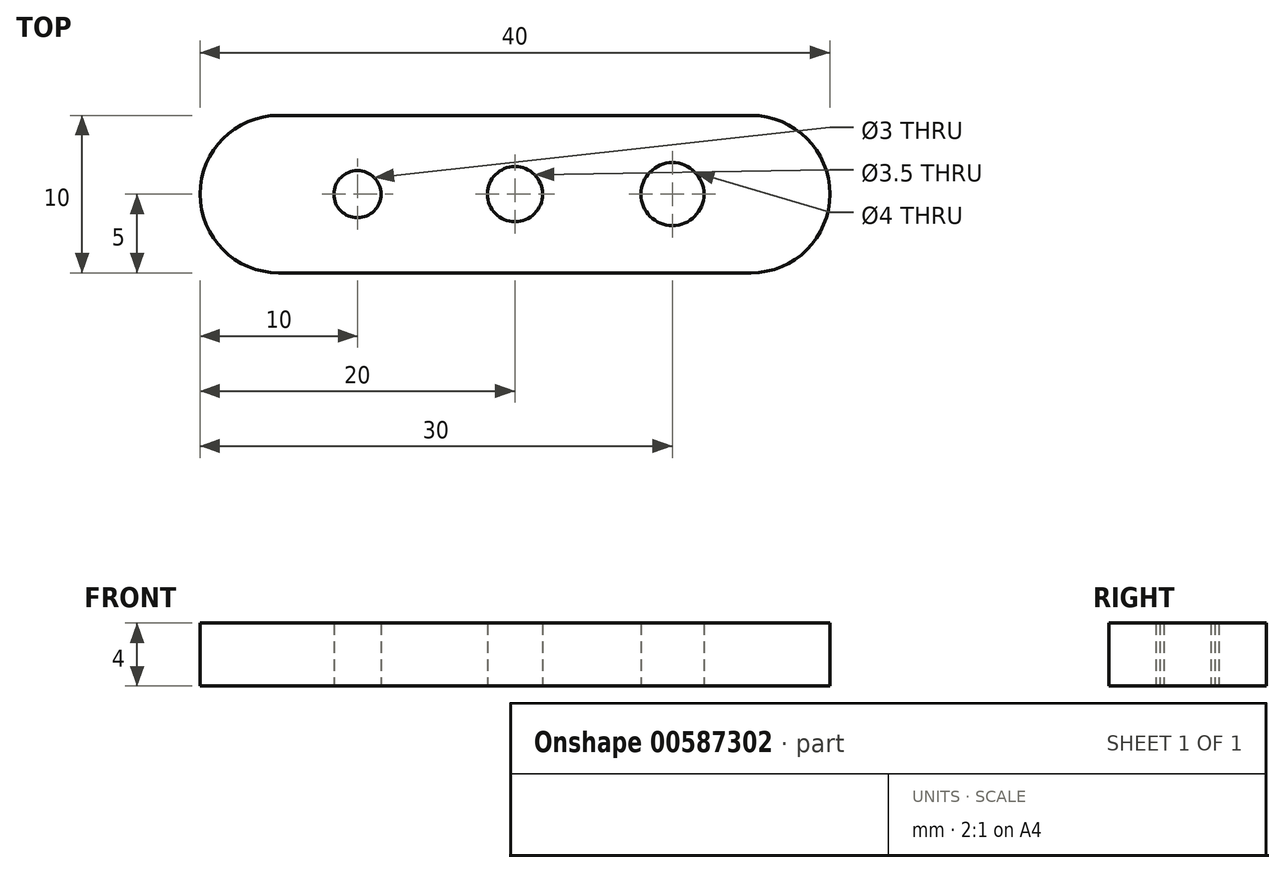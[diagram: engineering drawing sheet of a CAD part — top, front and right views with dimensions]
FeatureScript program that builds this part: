
annotation { "Feature Type Name" : "Feature", "Feature Type Description" : "" }
export const myFeature = defineFeature(function(context is Context, id is Id, definition is map)
    precondition{}
    {
        {
            var Q0;
            Q0=qCreatedBy(makeId("Top.planeOp"),FACE);
            var sketch = newSketch(context, id + "F0", { "sketchPlane" : qUnion([Q0])});
            skLineSegment(sketch, "E0.bottom", {"start": v(-20, 5) * mm, "end": v(20, 5) * mm});
            skLineSegment(sketch, "E0.top", {"start": v(-20, -5) * mm, "end": v(20, -5) * mm});
            skLineSegment(sketch, "E0.left", {"start": v(-20, 5) * mm, "end": v(-20, -5) * mm});
            skLineSegment(sketch, "E0.right", {"start": v(20, 5) * mm, "end": v(20, -5) * mm});
            skPoint(sketch, "E0.middle", {"position": v(0, 0) * mm});
            skCircle(sketch, "E1", {"center": v(-10, 0) * mm, "radius": 1.5 * mm});
            skCircle(sketch, "E2", {"center": v(0, 0) * mm, "radius": 1.75 * mm});
            skCircle(sketch, "E3", {"center": v(10, 0) * mm, "radius": 2 * mm});
            skSolve(sketch);
        }
        {
            var Q0;
            Q0=makeQuery(id+"F0.imprint","IMPRINT",FACE,{"disambiguationData":[TD([[makeQuery(id+"F0.imprint","IMPRINT",EDGE,{"derivedFrom":sQuery(id+"F0.wireOp",EDGE,"E0.bottom")}),-1.0]])]});
            extrude(context, id + "F1", {"entities" : qUnion([Q0]), "depth" : 4 * mm, "offsetDistance" : 25 * mm});
        }
        {
            var Q0;
            Q0=makeQuery(id+"F1.opExtrude","SWEPT_EDGE",EDGE,{"disambiguationData":[OSD([sQuery(id+"F0.wireOp",EDGE,"E0.bottom"),sQuery(id+"F0.wireOp",EDGE,"E0.left")])]});
            var Q1;
            Q1=makeQuery(id+"F1.opExtrude","SWEPT_EDGE",EDGE,{"disambiguationData":[OSD([sQuery(id+"F0.wireOp",EDGE,"E0.top"),sQuery(id+"F0.wireOp",EDGE,"E0.left")])]});
            var Q2;
            Q2=makeQuery(id+"F1.opExtrude","SWEPT_EDGE",EDGE,{"disambiguationData":[OSD([sQuery(id+"F0.wireOp",EDGE,"E0.top"),sQuery(id+"F0.wireOp",EDGE,"E0.right")])]});
            var Q3;
            Q3=makeQuery(id+"F1.opExtrude","SWEPT_EDGE",EDGE,{"disambiguationData":[OSD([sQuery(id+"F0.wireOp",EDGE,"E0.bottom"),sQuery(id+"F0.wireOp",EDGE,"E0.right")])]});
            fillet(context, id + "F2", {"entities" : qUnion([Q0, Q1, Q2, Q3]), "radius" : 5 * mm, "tangentPropagation" : true, "allowEdgeOverflow" : false});
        }
    });
